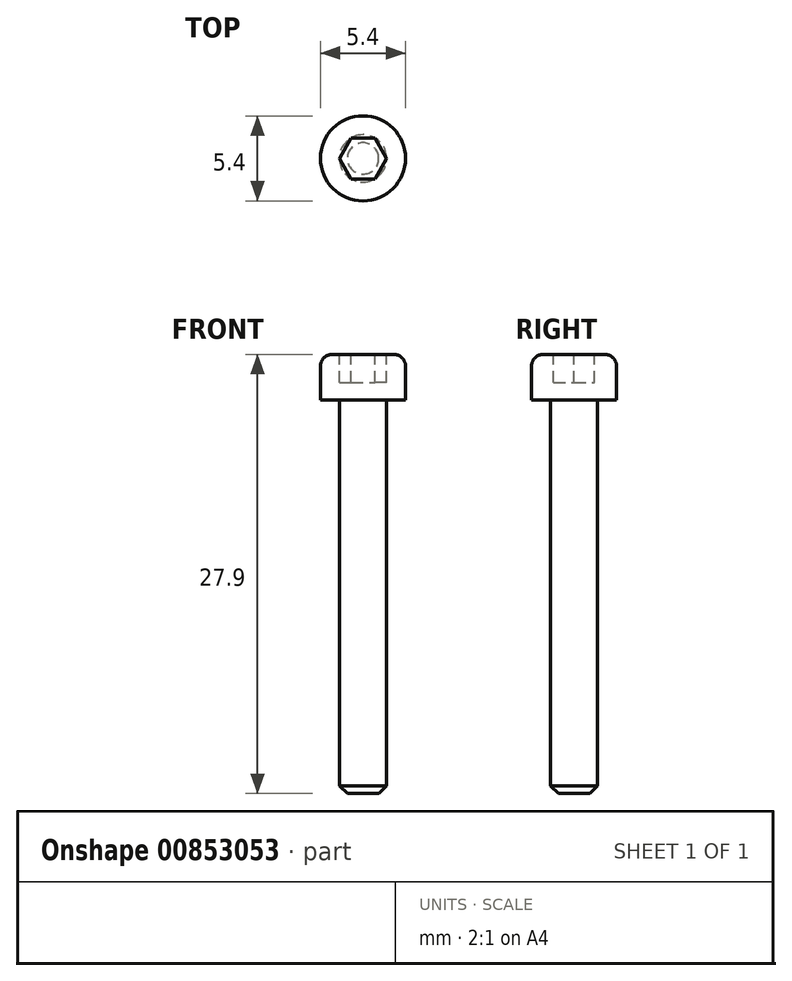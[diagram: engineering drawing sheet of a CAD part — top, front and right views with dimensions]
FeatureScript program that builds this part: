
annotation { "Feature Type Name" : "Feature", "Feature Type Description" : "" }
export const myFeature = defineFeature(function(context is Context, id is Id, definition is map)
    precondition{}
    {
        {
            var Q0;
            Q0=qCreatedBy(makeId("Front.planeOp"),FACE);
            var sketch = newSketch(context, id + "F0", { "sketchPlane" : qUnion([Q0])});
            skLineSegment(sketch, "E0", {"start": v(0, 0) * mm, "end": v(0, 27.9) * mm});
            skLineSegment(sketch, "E1", {"start": v(0, 27.9) * mm, "end": v(2.7, 27.9) * mm});
            skLineSegment(sketch, "E2", {"start": v(2.7, 27.9) * mm, "end": v(2.7, 25) * mm});
            skLineSegment(sketch, "E3", {"start": v(2.7, 25) * mm, "end": v(1.5, 25) * mm});
            skLineSegment(sketch, "E4", {"start": v(1.5, 25) * mm, "end": v(1.5, 0) * mm});
            skLineSegment(sketch, "E5", {"start": v(1.5, 0) * mm, "end": v(0, 0) * mm});
            skSolve(sketch);
        }
        {
            var Q0;
            Q0=qSketchRegion(id+"F0",true);
            var Q1;
            Q1=sQuery(id+"F0.wireOp",EDGE,"E0");
            revolve(context, id + "F1", {"surfaceOperationType" : NewSurfaceOperationType.NEW, "entities" : qUnion([Q0]), "axis" : qUnion([Q1]), "revolveType" : RevolveType.FULL});
        }
        {
            var Q0;
            Q0=makeQuery(id+"F1.opRevolve","SWEPT_FACE",FACE,{"disambiguationData":[OSD([sQuery(id+"F0.wireOp",EDGE,"E1")])]});
            var sketch = newSketch(context, id + "F2", { "sketchPlane" : qUnion([Q0])});
            skCircle(sketch, "E6.cCircle", {"center": v(0, 0) * mm, "radius": 1.3 * mm, "construction": true});
            skLineSegment(sketch, "E6.0", {"start": v(-0.75, 1.3) * mm, "end": v(0.75, 1.3) * mm});
            skLineSegment(sketch, "E6.1", {"start": v(0.75, 1.3) * mm, "end": v(1.5, 0) * mm});
            skLineSegment(sketch, "E6.2", {"start": v(1.5, 0) * mm, "end": v(0.75, -1.3) * mm});
            skLineSegment(sketch, "E6.3", {"start": v(0.75, -1.3) * mm, "end": v(-0.75, -1.3) * mm});
            skLineSegment(sketch, "E6.4", {"start": v(-0.75, -1.3) * mm, "end": v(-1.5, 0) * mm});
            skLineSegment(sketch, "E6.5", {"start": v(-1.5, 0) * mm, "end": v(-0.75, 1.3) * mm});
            skPoint(sketch, "E6.0.midPoint", {"position": v(0, 1.3) * mm});
            skSolve(sketch);
        }
        {
            var Q0;
            Q0=qSketchRegion(id+"F2",true);
            extrude(context, id + "F3", {"entities" : qUnion([Q0]), "operationType" : NewBodyOperationType.REMOVE, "oppositeDirection" : true, "depth" : 1.8 * mm, "offsetDistance" : 25 * mm});
        }
        {
            var Q0;
            Q0=makeQuery(id+"F1.opRevolve","SWEPT_EDGE",EDGE,{"disambiguationData":[OSD([sQuery(id+"F0.wireOp",EDGE,"E1"),sQuery(id+"F0.wireOp",EDGE,"E2")])]});
            fillet(context, id + "F4", {"entities" : qUnion([Q0]), "radius" : 0.75 * mm, "tangentPropagation" : true, "allowEdgeOverflow" : false});
        }
        {
            var Q0;
            Q0=makeQuery(id+"F1.opRevolve","SWEPT_EDGE",EDGE,{"disambiguationData":[OSD([sQuery(id+"F0.wireOp",EDGE,"E4"),sQuery(id+"F0.wireOp",EDGE,"E5")])]});
            chamfer(context, id + "F5", {"entities" : qUnion([Q0]), "width" : 0.5 * mm, "tangentPropagation" : true});
        }
    });
